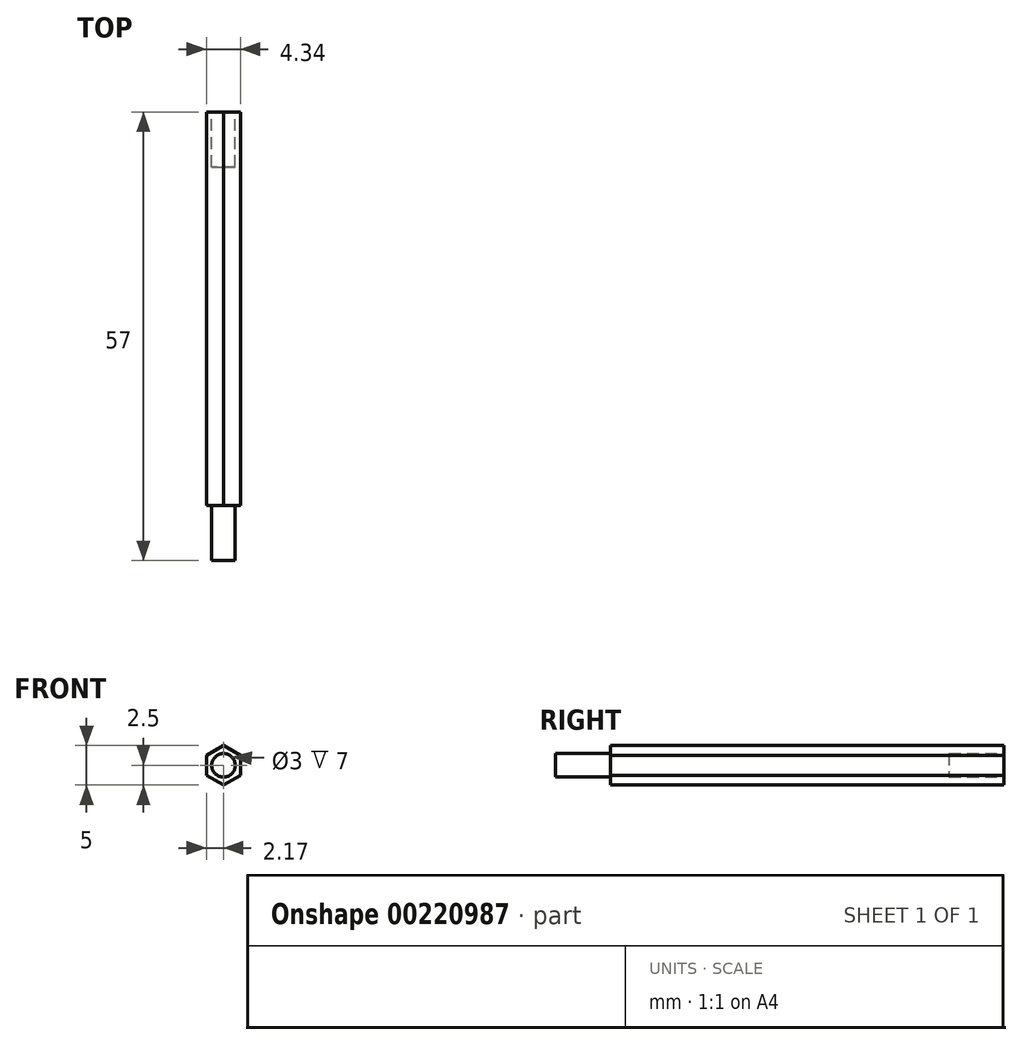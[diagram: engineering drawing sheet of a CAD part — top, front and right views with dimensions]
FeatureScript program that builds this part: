
annotation { "Feature Type Name" : "Feature", "Feature Type Description" : "" }
export const myFeature = defineFeature(function(context is Context, id is Id, definition is map)
    precondition{}
    {
        {
            var Q0;
            Q0=qCreatedBy(makeId("Front.planeOp"),FACE);
            var sketch = newSketch(context, id + "F0", { "sketchPlane" : qUnion([Q0])});
            skLineSegment(sketch, "E0", {"start": v(0, 0) * mm, "end": v(0, 2.5) * mm});
            skLineSegment(sketch, "E1", {"start": v(0, 0) * mm, "end": v(0, -2.5) * mm});
            skLineSegment(sketch, "E2", {"start": v(0, 0) * mm, "end": v(2.17, 1.25) * mm});
            skLineSegment(sketch, "E3", {"start": v(0, 0) * mm, "end": v(2.17, -1.25) * mm});
            skLineSegment(sketch, "E4", {"start": v(0, 0) * mm, "end": v(-2.17, -1.25) * mm});
            skLineSegment(sketch, "E5", {"start": v(0, 0) * mm, "end": v(-2.17, 1.25) * mm});
            skLineSegment(sketch, "E6", {"start": v(-2.17, 1.25) * mm, "end": v(0, 2.5) * mm});
            skLineSegment(sketch, "E7", {"start": v(0, 2.5) * mm, "end": v(2.17, 1.25) * mm});
            skLineSegment(sketch, "E8", {"start": v(2.17, 1.25) * mm, "end": v(2.17, -1.25) * mm});
            skLineSegment(sketch, "E9", {"start": v(2.17, -1.25) * mm, "end": v(0, -2.5) * mm});
            skLineSegment(sketch, "E10", {"start": v(0, -2.5) * mm, "end": v(-2.17, -1.25) * mm});
            skLineSegment(sketch, "E11", {"start": v(-2.17, -1.25) * mm, "end": v(-2.17, 1.25) * mm});
            skSolve(sketch);
        }
        {
            var Q0;
            Q0=qSketchRegion(id+"F0",true);
            extrude(context, id + "F1", {"entities" : qUnion([Q0]), "depth" : 50 * mm});
        }
        {
            var Q0;
            Q0=makeQuery(id+"F1.opExtrude","CAP_FACE",FACE,{"disambiguationData":[OSD([sQuery(id+"F0.wireOp",EDGE,"E6"),sQuery(id+"F0.wireOp",EDGE,"E7"),sQuery(id+"F0.wireOp",EDGE,"E8"),sQuery(id+"F0.wireOp",EDGE,"E9"),sQuery(id+"F0.wireOp",EDGE,"E10"),sQuery(id+"F0.wireOp",EDGE,"E11")])],"isStart":false});
            var sketch = newSketch(context, id + "F2", { "sketchPlane" : qUnion([Q0])});
            skCircle(sketch, "E12", {"center": v(0, 0) * mm, "radius": 1.5 * mm});
            skSolve(sketch);
        }
        {
            var Q0;
            Q0=qSketchRegion(id+"F2",true);
            extrude(context, id + "F3", {"entities" : qUnion([Q0]), "operationType" : NewBodyOperationType.ADD, "depth" : 7 * mm});
        }
        {
            var Q0;
            Q0=makeQuery(id+"F1.opExtrude","CAP_FACE",FACE,{"disambiguationData":[OSD([sQuery(id+"F0.wireOp",EDGE,"E6"),sQuery(id+"F0.wireOp",EDGE,"E7"),sQuery(id+"F0.wireOp",EDGE,"E8"),sQuery(id+"F0.wireOp",EDGE,"E9"),sQuery(id+"F0.wireOp",EDGE,"E10"),sQuery(id+"F0.wireOp",EDGE,"E11")])],"isStart":true});
            var sketch = newSketch(context, id + "F4", { "sketchPlane" : qUnion([Q0])});
            skCircle(sketch, "E13", {"center": v(0, 0) * mm, "radius": 1.5 * mm});
            skSolve(sketch);
        }
        {
            var Q0;
            Q0=qSketchRegion(id+"F4",true);
            extrude(context, id + "F5", {"entities" : qUnion([Q0]), "operationType" : NewBodyOperationType.REMOVE, "oppositeDirection" : true, "depth" : 7 * mm});
        }
    });
